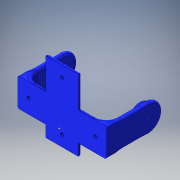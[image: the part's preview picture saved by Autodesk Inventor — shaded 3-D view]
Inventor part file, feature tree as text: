
AUTODESK INVENTOR PART (.ipt)
format: ipt  version: 2016 (Build 200138000, 138)  size: 483,328 bytes
history: native  units: in
note: dims shown in document units (in); Inventor stores cm internally (conversion verified against a paired STEP export)
features: sketch x11, fillet x10, extrude x9, hole x2
ambient origin geometry x8: Origin, YZ Plane, XZ Plane, XY Plane, X Axis, Y Axis, Z Axis, Center Point
bodies: Solid1 (feature_tree)
feature tree (32):
  extrude  "Extrusion1"  Depth=0.5197in
  extrude  "Extrusion3"  Depth=0.0787in
  sketch  "Sketch5"  dims[d9=0.9449in d10=0.0in d11=0.2835in]
  extrude  "Extrusion4"  Depth=0.2835in
  extrude  "Extrusion5"  Depth=0.2598in
  fillet  "Fillet1"  Radius=0.2598in
  fillet  "Fillet4"  Radius=0.5197in
  fillet  "Fillet5"  Radius=0.3622in
  fillet  "Fillet6"  Radius=0.1437in
  fillet  "Fillet7"  Radius=0.5551in
  extrude  "Extrusion6"  Depth=0.0787in TaperAngle=0.0deg
  fillet  "Fillet8"  Radius=0.0787in
  sketch  "Sketch9"  dims[d19=0.2224in d24=0.0787in d25=0.0in d26=0.0787in]
  extrude  "Extrusion7"  Depth=0.0787in TaperAngle=0.0deg
  fillet  "Fillet10"  Radius=0.1969in
  fillet  "Fillet11"  Radius=0.0394in
  sketch  "Sketch10"  dims[d27=0.0787in d28=0.0787in d29=0.0in d30=0.1969in d33=0.0394in]
  extrude  "Extrusion8"  Depth=0.0394in
  extrude  "Extrusion10"  Depth=0.0197in
  extrude  "Extrusion11"  Depth=0.1969in
  hole  "Hole2"  [1 undecoded]
  fillet  "Fillet15"  Radius=0.2598in
  fillet  "Fillet16"  Radius=0.1181in
  sketch  "Sketch18"  dims[d43=0.2598in d44=0.2598in d45=0.2598in d46=0.1181in]
  hole  "Hole3"  [1 undecoded]
  sketch  "Sketch1"  dims[d0=1.6142in d1=0.5197in]
  sketch  "Sketch4"  dims[d2=0.0787in d3=0.0in d8=0.0787in]
  sketch  "Sketch7"  dims[d12=0.2598in d13=0.2598in d14=0.2598in d15=0.5197in d16=0.3622in d17=0.1437in d18=0.5551in]
  sketch  "Sketch15"  dims[d34=0.0394in d35=0.0394in]
  sketch  "Sketch16"  dims[d36=0.0197in d37=0.0787in]
  sketch  "Sketch17"  dims[d38=0.9449in d39=0.0in d40=0.1969in]
  sketch  "Sketch19"  dims[d47=0.1181in d48=0.0in d49=0.0394in d50=0.0394in d51=0.1181in d52=0.1181in d53=0.0in d79=0.5118in d80=0.5118in d81=0.2096in d82=0.0in d83=0.5118in d84=0.5118in d85=0.562in d86=0.0in d87=0.2953in d88=0.2953in d89=0.2598in d90=0.2598in d91=0.1969in d92=0.1969in d93=0.2953in d94=0.2953in d95=0.1969in d96=0.2598in d97=0.2598in d98=0.1969in d99=0.0591in d100=0.2362in d101=0.1575in d102=0.0787in d103=90.0deg d104=0.1181in d105=0.8108in d106=0.0748in d107=0.0354in d108=0.0394in d109=0.2362in d110=0.1575in d111=0.0787in d112=90.0deg d113=0.315in d114=0.8108in]
note: 2 required parameter values undecoded (feature->parameter linkage not recoverable at this tier; creation-order binding heuristic only, values carry confidence <= 0.55)
